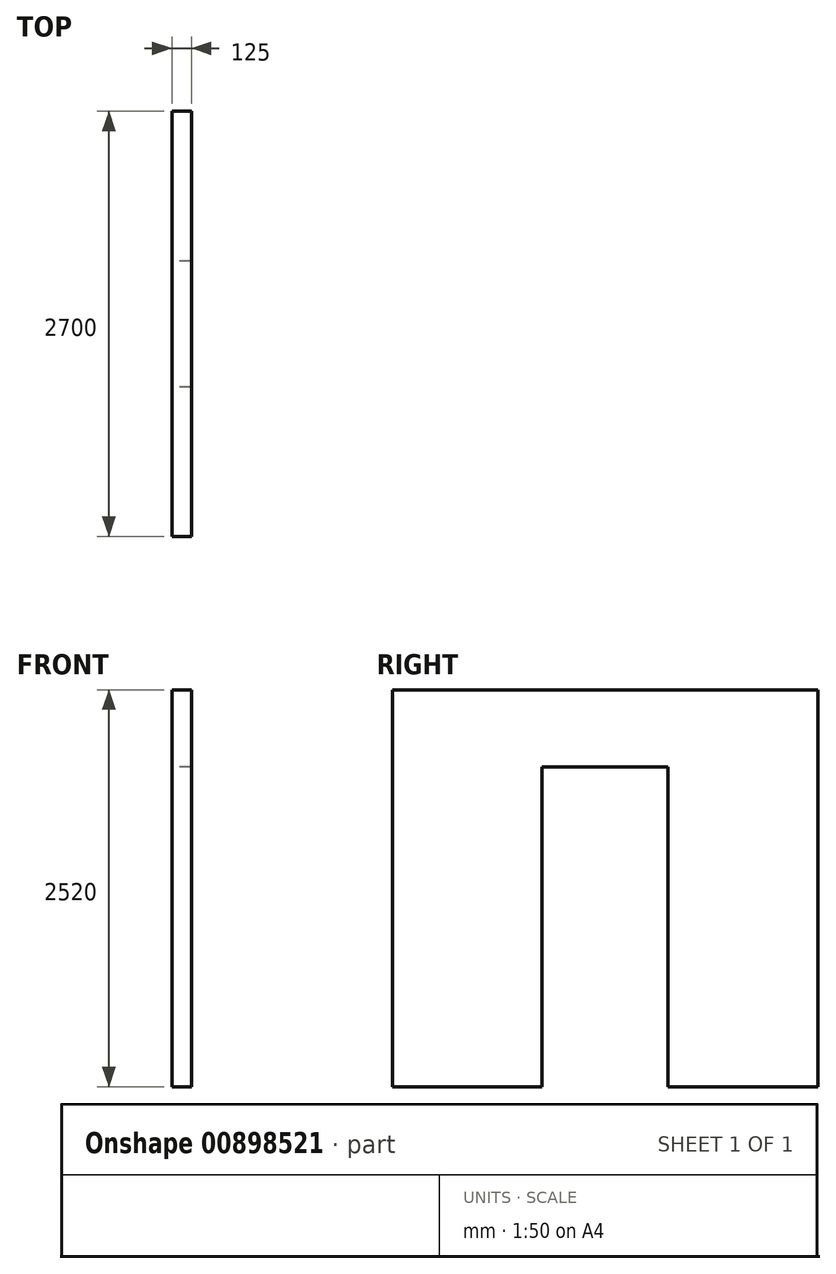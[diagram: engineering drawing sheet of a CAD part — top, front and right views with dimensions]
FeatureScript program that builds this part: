
annotation { "Feature Type Name" : "Feature", "Feature Type Description" : "" }
export const myFeature = defineFeature(function(context is Context, id is Id, definition is map)
    precondition{}
    {
        {
            var Q0;
            Q0=qCreatedBy(makeId("Right.planeOp"),FACE);
            var sketch = newSketch(context, id + "F0", { "sketchPlane" : qUnion([Q0])});
            skLineSegment(sketch, "E0.bottom", {"start": v(-1350, 0) * mm, "end": v(-400, 0) * mm});
            skLineSegment(sketch, "E0.top", {"start": v(-1350, 2520) * mm, "end": v(1350, 2520) * mm});
            skLineSegment(sketch, "E0.left", {"start": v(-1350, 0) * mm, "end": v(-1350, 2520) * mm});
            skLineSegment(sketch, "E0.right", {"start": v(1350, 0) * mm, "end": v(1350, 2520) * mm});
            skLineSegment(sketch, "E1.top", {"start": v(-400, 2030) * mm, "end": v(400, 2030) * mm});
            skLineSegment(sketch, "E1.left", {"start": v(-400, 0) * mm, "end": v(-400, 2030) * mm});
            skLineSegment(sketch, "E1.right", {"start": v(400, 0) * mm, "end": v(400, 2030) * mm});
            skLineSegment(sketch, "E2.trimOffspring", {"start": v(400, 0) * mm, "end": v(1350, 0) * mm});
            skSolve(sketch);
        }
        {
            var Q0;
            Q0=makeQuery(id+"F0.imprint","IMPRINT",FACE,{"disambiguationData":[TD([[makeQuery(id+"F0.imprint","IMPRINT",EDGE,{"derivedFrom":sQuery(id+"F0.wireOp",EDGE,"E0.bottom")}),1.0]])]});
            extrude(context, id + "F1", {"entities" : qUnion([Q0]), "depth" : 125 * mm, "offsetDistance" : 25 * mm});
        }
    });
